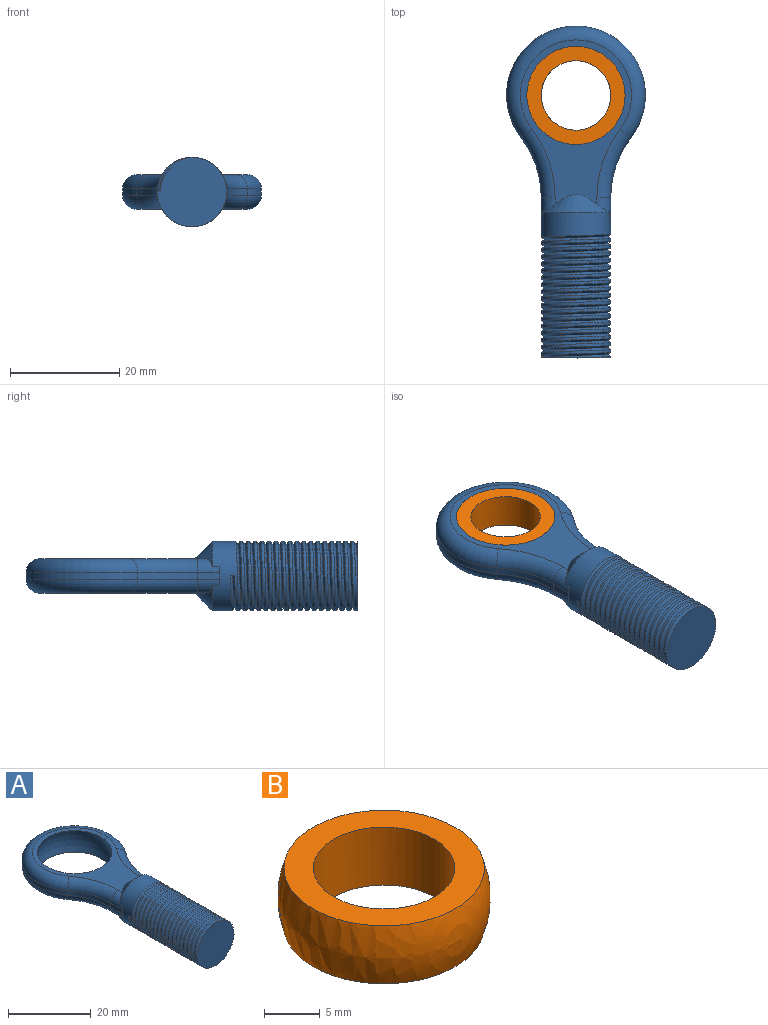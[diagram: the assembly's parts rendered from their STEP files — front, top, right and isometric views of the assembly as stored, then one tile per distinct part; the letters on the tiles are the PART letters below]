
ASSEMBLY  parts=2 mates=1
PART A: 49 faces, bbox 27.5x62.1x14.7 mm
  f0: cylinder r=6.35mm len=12.7mm, axis (0,-1,0), area 159.4mm2, adj f18,f20,f21,f22,f23,f24,f26,f35
  f1: cylinder r=6.35mm len=9.53mm, axis (0,-1,0), area 2.8mm2, adj f2,f42,f48
  f2: cylinder r=6.35mm len=12.7mm, axis (0,-1,0), area 23.2mm2, adj f1,f3,f42,f46,f47,f48
  f3: cylinder r=6.35mm len=12.7mm, axis (0,-1,0), area 20.3mm2, adj f2,f4,f47,f48
  f4: cylinder r=6.35mm len=12.7mm, axis (0,-1,0), area 20.3mm2, adj f3,f5,f47,f48
  f5: cylinder r=6.35mm len=12.7mm, axis (0,-1,0), area 20.3mm2, adj f4,f6,f47,f48
  f6: cylinder r=6.35mm len=12.7mm, axis (0,-1,0), area 20.3mm2, adj f5,f7,f47,f48
  f7: cylinder r=6.35mm len=12.7mm, axis (0,-1,0), area 20.3mm2, adj f6,f8,f47,f48
  f8: cylinder r=6.35mm len=12.7mm, axis (0,-1,0), area 20.3mm2, adj f7,f9,f47,f48
  f9: cylinder r=6.35mm len=12.7mm, axis (0,-1,0), area 20.3mm2, adj f8,f10,f47,f48
  f10: cylinder r=6.35mm len=12.7mm, axis (0,-1,0), area 20.3mm2, adj f9,f11,f47,f48
  f11: cylinder r=6.35mm len=12.7mm, axis (0,-1,0), area 20.3mm2, adj f10,f12,f47,f48
  f12: cylinder r=6.35mm len=12.7mm, axis (0,-1,0), area 20.3mm2, adj f11,f13,f47,f48
  f13: cylinder r=6.35mm len=12.7mm, axis (0,-1,0), area 20.3mm2, adj f12,f14,f47,f48
  f14: cylinder r=6.35mm len=12.7mm, axis (0,-1,0), area 20.3mm2, adj f13,f15,f47,f48
  f15: cylinder r=6.35mm len=12.7mm, axis (0,-1,0), area 20.3mm2, adj f14,f16,f47,f48
  f16: cylinder r=6.35mm len=12.7mm, axis (0,-1,0), area 20.3mm2, adj f15,f17,f47,f48
  f17: cylinder r=6.35mm len=12.7mm, axis (0,-1,0), area 20.3mm2, adj f16,f18,f47,f48
  f18: cylinder r=6.35mm len=12.7mm, axis (0,-1,0), area 20.3mm2, adj f0,f17,f47,f48
  f19: plane 30.09x20.32mm, normal (0,0,-1), area 157.9mm2, adj f20,f32,f33,f34,f35,f40,f44
  f20: cylinder r=2.54mm len=3.89mm, axis (0,1,0), area 9.8mm2, adj f0,f19,f23,f31,f32,f44
  f21: plane 1.69x0.23mm, normal (0,-1,0), area 0mm2, adj f0,f30,f39
  f22: plane 1.69x0.23mm, normal (0,-1,0), area 0mm2, adj f0,f30,f35
  f23: plane 1.69x0.23mm, normal (0,-1,0), area 0mm2, adj f0,f20,f31
  f24: plane 1.69x0.23mm, normal (0,-1,0), area 0mm2, adj f0,f26,f31
  f25: plane 30.09x20.32mm, normal (0,0,1), area 156.1mm2, adj f26,f36,f37,f38,f39,f41,f43
  f26: cylinder r=2.54mm len=3.89mm, axis (0,-1,0), area 9.8mm2, adj f0,f24,f25,f31,f36,f43
  f27: cylinder r=18mm len=10.96mm, axis (0,0,-1), area 15mm2, adj f28,f31,f32,f36
  f28: cylinder r=12.7mm len=25.4mm, axis (0,0,-1), area 71.8mm2, adj f27,f29,f33,f37
  f29: cylinder r=18mm len=10.96mm, axis (0,0,-1), area 15mm2, adj f28,f30,f34,f38
  f30: plane 3.89x1.27mm, normal (-1,0,0), area 4.9mm2, adj f21,f22,f29,f35,f39
  f31: plane 3.89x1.27mm, normal (1,0,0), area 4.9mm2, adj f20,f23,f24,f26,f27
  f32: torus R=20.54mm, axis (0,0,1), area 49.4mm2, adj f19,f20,f27,f33
  f33: torus R=10.16mm, axis (0,0,1), area 209.2mm2, adj f19,f28,f32,f34
  f34: torus R=20.54mm, axis (0,0,1), area 49.4mm2, adj f19,f29,f33,f35
  f35: cylinder r=2.54mm len=3.89mm, axis (0,-1,0), area 9.8mm2, adj f0,f19,f22,f30,f34,f44
  f36: torus R=20.54mm, axis (0,0,1), area 49.4mm2, adj f25,f26,f27,f37
  f37: torus R=10.16mm, axis (0,0,1), area 209.2mm2, adj f25,f28,f36,f38
  f38: torus R=20.54mm, axis (0,0,1), area 49.4mm2, adj f25,f29,f37,f39
  f39: cylinder r=2.54mm len=3.89mm, axis (0,1,0), area 9.8mm2, adj f0,f21,f25,f30,f38,f43
  f40: cone r=2.64mm half-angle=79.8deg, axis (0,0,1), area 1.9mm2, adj f19,f41
  f41: sphere r=9.53mm, area 379.7mm2, adj f25,f40
  f42: plane 12.7x12.7mm, normal (0,-1,0), area 124.4mm2, adj f1,f2,f46,f48
  f43: cone r=6.35mm half-angle=45deg, axis (0,-1,0), area 37.8mm2, adj f0,f25,f26,f39
  f44: cone r=6.35mm half-angle=45deg, axis (0,-1,0), area 37.8mm2, adj f0,f19,f20,f35
  f45: plane 0.76x0.57mm, normal (0.5,0,-0.87), area 0.3mm2, adj f0,f47,f48
  f46: plane 0.57x0.44mm, normal (-0.5,0,0.87), area 0.2mm2, adj f2,f42,f47,f48
  f47: bspline ~23.24x14.66mm, area 470mm2, adj f0,f2,f3,f4,f5,f6,f7,f8
  f48: bspline ~23.24x14.66mm, area 459.1mm2, adj f0,f1,f2,f3,f4,f5,f6,f7
PART B: 4 faces, bbox 19.1x19.1x19.1 mm
  f0: cylinder r=6.35mm len=12.7mm, axis (0,0,1), area 253.4mm2, adj f1,f2
  f1: plane 17.96x17.96mm, normal (0,0,-1), area 126.8mm2, adj f0,f3
  f2: plane 17.96x17.96mm, normal (0,0,1), area 126.6mm2, adj f0,f3
  f3: sphere r=9.53mm, area 380.1mm2, adj f1,f2
PLACE A t=(17.41,-16.94,13.48)mm
PLACE B t=(17.41,21.16,16.66)mm
MATE ball A.f40 <-> B.f0  axis (0,0,1) through (17.41,21.16,16.66)mm
